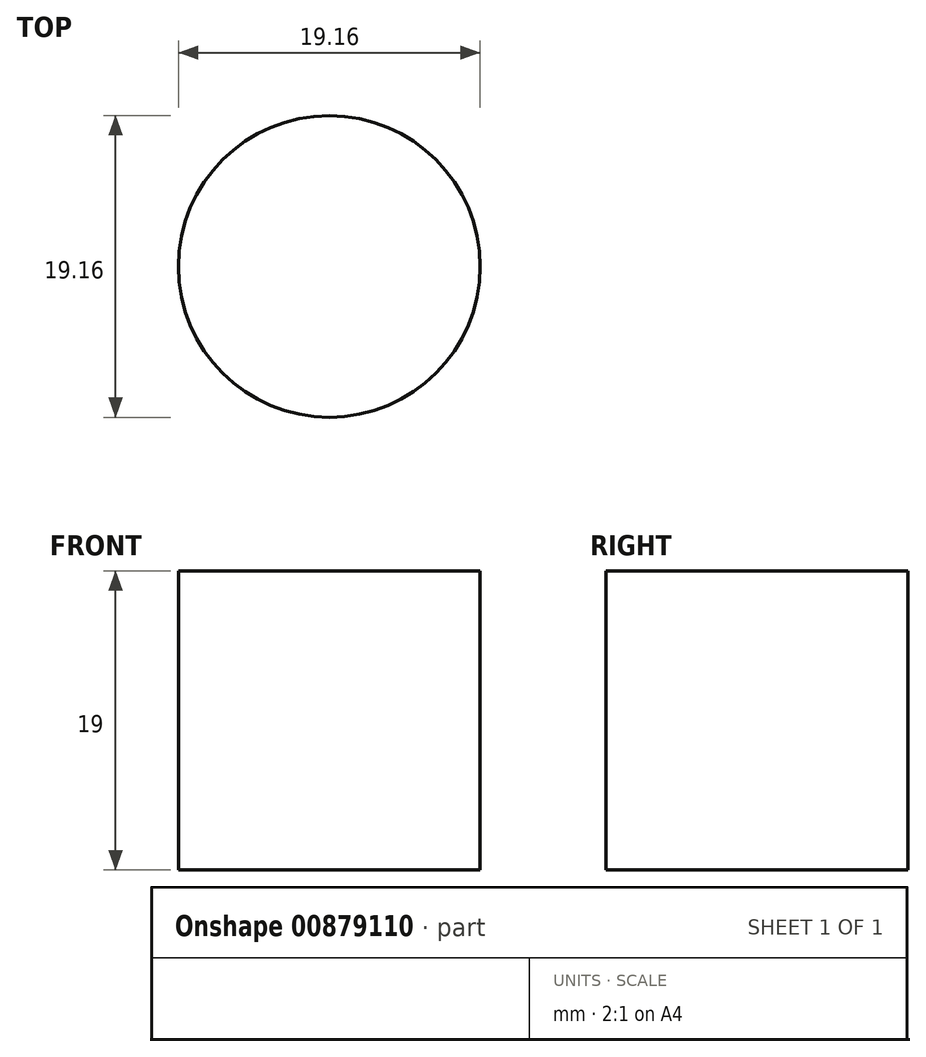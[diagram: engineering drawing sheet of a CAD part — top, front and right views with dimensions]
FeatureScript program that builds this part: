
annotation { "Feature Type Name" : "Feature", "Feature Type Description" : "" }
export const myFeature = defineFeature(function(context is Context, id is Id, definition is map)
    precondition{}
    {
        {
            var Q0;
            Q0=qCreatedBy(makeId("Top.planeOp"),FACE);
            var sketch = newSketch(context, id + "F0", { "sketchPlane" : qUnion([Q0])});
            skCircle(sketch, "E0", {"center": v(0, 0) * mm, "radius": 9.58 * mm});
            skSolve(sketch);
        }
        {
            var Q0;
            Q0=makeQuery(id+"F0.imprint","IMPRINT",FACE,{"disambiguationData":[TD([[makeQuery(id+"F0.imprint","IMPRINT",EDGE,{"derivedFrom":sQuery(id+"F0.wireOp",EDGE,"E0")}),1.0]])]});
            extrude(context, id + "F1", {"entities" : qUnion([Q0]), "depth" : 19 * mm, "offsetDistance" : 25 * mm});
        }
    });
